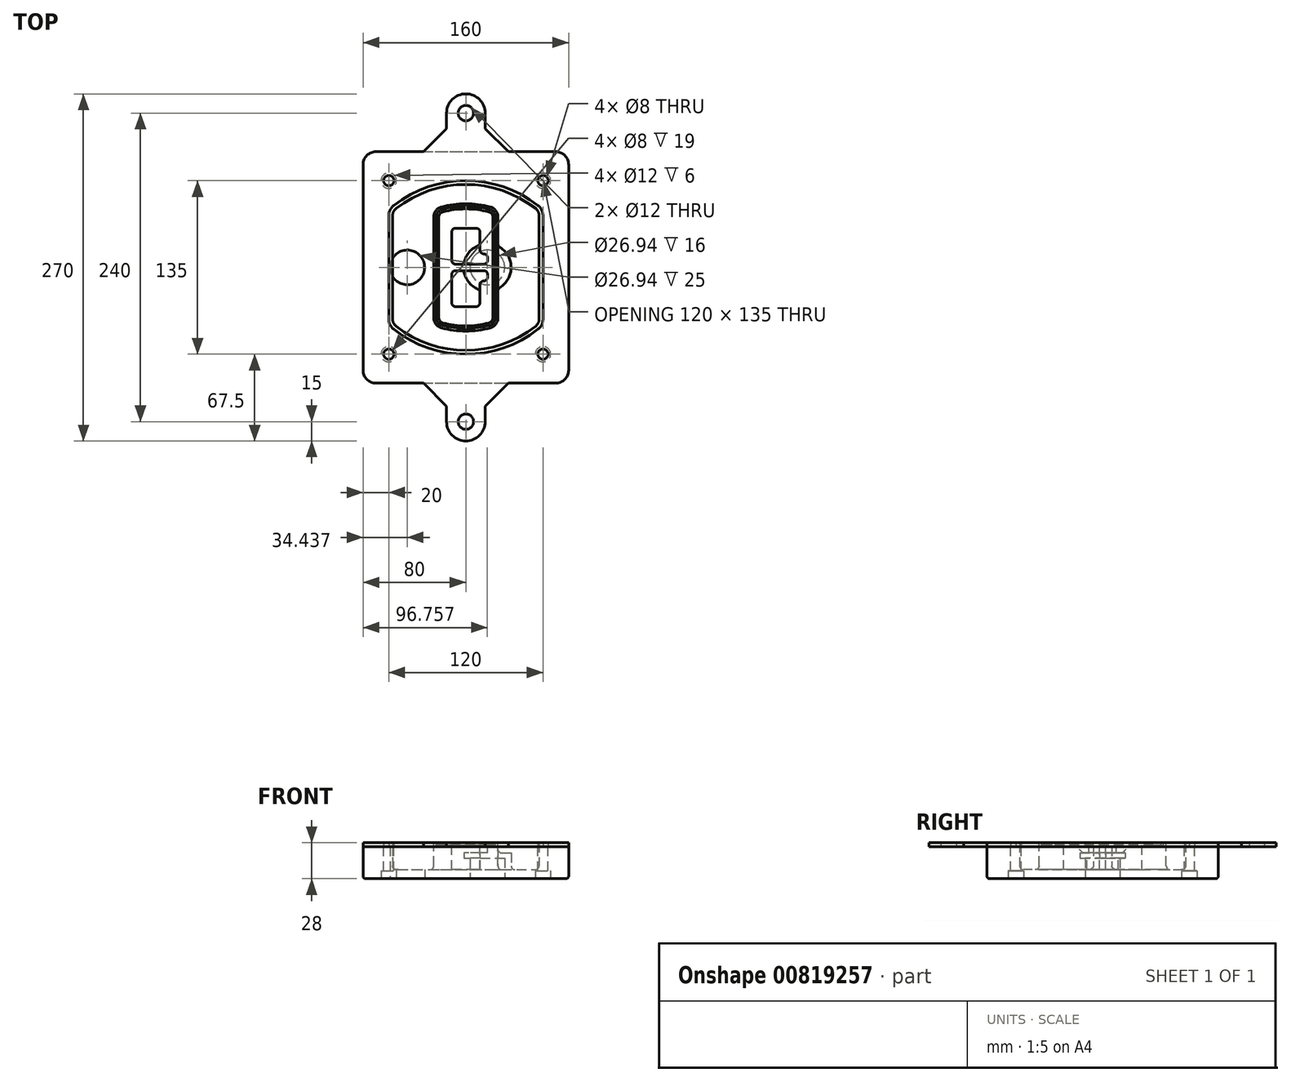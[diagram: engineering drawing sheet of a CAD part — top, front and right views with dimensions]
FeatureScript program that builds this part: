
annotation { "Feature Type Name" : "Feature", "Feature Type Description" : "" }
export const myFeature = defineFeature(function(context is Context, id is Id, definition is map)
    precondition{}
    {
        {
            var Q0;
            Q0=qCreatedBy(makeId("Top.planeOp"),FACE);
            var sketch = newSketch(context, id + "F0", { "sketchPlane" : qUnion([Q0])});
            skPoint(sketch, "E0.rect.middle", {"position": v(0, 0) * mm});
            skLineSegment(sketch, "E1.bottom", {"start": v(-70, -90) * mm, "end": v(70, -90) * mm});
            skLineSegment(sketch, "E1.top", {"start": v(-70, 90) * mm, "end": v(70, 90) * mm});
            skLineSegment(sketch, "E1.left", {"start": v(-80, -80) * mm, "end": v(-80, 80) * mm});
            skLineSegment(sketch, "E1.right", {"start": v(80, -80) * mm, "end": v(80, 80) * mm});
            skLineSegment(sketch, "E2", {"start": v(-80, 90) * mm, "end": v(80, -90) * mm, "construction": true});
            skLineSegment(sketch, "E3", {"start": v(80, 90) * mm, "end": v(-80, -90) * mm, "construction": true});
            skCircle(sketch, "E4", {"center": v(-60, 67.5) * mm, "radius": 4 * mm});
            skCircle(sketch, "E5", {"center": v(60, 67.5) * mm, "radius": 4 * mm});
            skCircle(sketch, "E6", {"center": v(60, -67.5) * mm, "radius": 4 * mm});
            skCircle(sketch, "E7", {"center": v(-60, -67.5) * mm, "radius": 4 * mm});
            skLineSegment(sketch, "E8", {"start": v(-60, 67.5) * mm, "end": v(60, 67.5) * mm, "construction": true});
            skLineSegment(sketch, "E9", {"start": v(60, 67.5) * mm, "end": v(60, -67.5) * mm, "construction": true});
            skLineSegment(sketch, "E10", {"start": v(60, -67.5) * mm, "end": v(-60, -67.5) * mm, "construction": true});
            skLineSegment(sketch, "E11", {"start": v(-60, -67.5) * mm, "end": v(-60, 67.5) * mm, "construction": true});
            skLineSegment(sketch, "E12", {"start": v(-60, 40.3) * mm, "end": v(-60, -40.3) * mm});
            skLineSegment(sketch, "E13", {"start": v(60, 40.3) * mm, "end": v(60, -40.3) * mm});
            skArc(sketch, "E14", {"start": v(56.15, 48.18) * mm, "mid": v(0, 67.5) * mm, "end": v(-56.15, 48.18) * mm});
            skArc(sketch, "E15", {"start": v(-56.15, -48.18) * mm, "mid": v(0, -67.5) * mm, "end": v(56.15, -48.18) * mm});
            skLineSegment(sketch, "E16", {"start": v(-60, 0) * mm, "end": v(60, 0) * mm, "construction": true});
            skPoint(sketch, "E17.visualSharp", {"position": v(-60, -45) * mm});
            skArc(sketch, "E17.filletArc", {"start": v(-60, -40.3) * mm, "mid": v(-58.99, -44.68) * mm, "end": v(-56.15, -48.18) * mm});
            skPoint(sketch, "E18.visualSharp", {"position": v(-60, 45) * mm});
            skArc(sketch, "E18.filletArc", {"start": v(-56.15, 48.18) * mm, "mid": v(-58.99, 44.68) * mm, "end": v(-60, 40.3) * mm});
            skPoint(sketch, "E19.visualSharp", {"position": v(60, 45) * mm});
            skArc(sketch, "E19.filletArc", {"start": v(60, 40.3) * mm, "mid": v(58.99, 44.68) * mm, "end": v(56.15, 48.18) * mm});
            skPoint(sketch, "E20.visualSharp", {"position": v(60, -45) * mm});
            skArc(sketch, "E20.filletArc", {"start": v(56.15, -48.18) * mm, "mid": v(58.99, -44.68) * mm, "end": v(60, -40.3) * mm});
            skPoint(sketch, "E21.visualSharp", {"position": v(-80, 90) * mm});
            skArc(sketch, "E21.filletArc", {"start": v(-70, 90) * mm, "mid": v(-77.07, 87.07) * mm, "end": v(-80, 80) * mm});
            skPoint(sketch, "E22.visualSharp", {"position": v(80, 90) * mm});
            skArc(sketch, "E22.filletArc", {"start": v(80, 80) * mm, "mid": v(77.07, 87.07) * mm, "end": v(70, 90) * mm});
            skPoint(sketch, "E23.visualSharp", {"position": v(80, -90) * mm});
            skArc(sketch, "E23.filletArc", {"start": v(70, -90) * mm, "mid": v(77.07, -87.07) * mm, "end": v(80, -80) * mm});
            skPoint(sketch, "E24.visualSharp", {"position": v(-80, -90) * mm});
            skArc(sketch, "E24.filletArc", {"start": v(-80, -80) * mm, "mid": v(-77.07, -87.07) * mm, "end": v(-70, -90) * mm});
            skArc(sketch, "E25.0", {"start": v(57, 40.3) * mm, "mid": v(56.3, 43.36) * mm, "end": v(54.3, 45.81) * mm});
            skLineSegment(sketch, "E25.1", {"start": v(57, 40.3) * mm, "end": v(57, -40.3) * mm});
            skArc(sketch, "E25.2", {"start": v(54.3, -45.81) * mm, "mid": v(56.3, -43.36) * mm, "end": v(57, -40.3) * mm});
            skArc(sketch, "E25.3", {"start": v(-54.3, -45.81) * mm, "mid": v(0, -64.5) * mm, "end": v(54.3, -45.81) * mm});
            skArc(sketch, "E25.4", {"start": v(-57, -40.3) * mm, "mid": v(-56.3, -43.36) * mm, "end": v(-54.3, -45.81) * mm});
            skArc(sketch, "E25.5", {"start": v(54.3, 45.81) * mm, "mid": v(0, 64.5) * mm, "end": v(-54.3, 45.81) * mm});
            skLineSegment(sketch, "E25.6", {"start": v(-57, 40.3) * mm, "end": v(-57, -40.3) * mm});
            skArc(sketch, "E25.7", {"start": v(-54.3, 45.81) * mm, "mid": v(-56.3, 43.36) * mm, "end": v(-57, 40.3) * mm});
            skArc(sketch, "E26.0", {"start": v(-58.62, 51.33) * mm, "mid": v(-62.58, 46.43) * mm, "end": v(-64, 40.3) * mm});
            skArc(sketch, "E26.1", {"start": v(58.62, 51.33) * mm, "mid": v(0, 71.5) * mm, "end": v(-58.62, 51.33) * mm});
            skArc(sketch, "E26.2", {"start": v(64, 40.3) * mm, "mid": v(62.58, 46.43) * mm, "end": v(58.62, 51.33) * mm});
            skLineSegment(sketch, "E26.3", {"start": v(64, 40.3) * mm, "end": v(64, -40.3) * mm});
            skArc(sketch, "E26.4", {"start": v(58.62, -51.33) * mm, "mid": v(62.58, -46.43) * mm, "end": v(64, -40.3) * mm});
            skLineSegment(sketch, "E26.5", {"start": v(-64, 40.3) * mm, "end": v(-64, -40.3) * mm});
            skArc(sketch, "E26.6", {"start": v(-58.62, -51.33) * mm, "mid": v(0, -71.5) * mm, "end": v(58.62, -51.33) * mm});
            skArc(sketch, "E26.7", {"start": v(-64, -40.3) * mm, "mid": v(-62.58, -46.43) * mm, "end": v(-58.62, -51.33) * mm});
            skSolve(sketch);
        }
        {
            var Q0;
            Q0=makeQuery(id+"F0.imprint","IMPRINT",FACE,{"disambiguationData":[TD([[makeQuery(id+"F0.imprint","IMPRINT",EDGE,{"derivedFrom":sQuery(id+"F0.wireOp",EDGE,"E1.bottom")}),1.0]])]});
            var Q1;
            Q1=makeQuery(id+"F0.imprint","IMPRINT",FACE,{"disambiguationData":[TD([[makeQuery(id+"F0.imprint","IMPRINT",EDGE,{"derivedFrom":sQuery(id+"F0.wireOp",EDGE,"E12")}),1.0]])]});
            var Q2;
            Q2=makeQuery(id+"F0.imprint","IMPRINT",FACE,{"disambiguationData":[TD([[makeQuery(id+"F0.imprint","IMPRINT",EDGE,{"derivedFrom":sQuery(id+"F0.wireOp",EDGE,"E25.0")}),1.0]])]});
            var Q3;
            Q3=makeQuery(id+"F0.imprint","IMPRINT",FACE,{"disambiguationData":[TD([[makeQuery(id+"F0.imprint","IMPRINT",EDGE,{"derivedFrom":sQuery(id+"F0.wireOp",EDGE,"E12")}),-1.0]])]});
            extrude(context, id + "F1", {"entities" : qUnion([Q0, Q1, Q2, Q3]), "oppositeDirection" : true, "depth" : 25 * mm});
        }
        {
            var Q0;
            Q0=makeQuery(id+"F0.imprint","IMPRINT",FACE,{"disambiguationData":[TD([[makeQuery(id+"F0.imprint","IMPRINT",EDGE,{"derivedFrom":sQuery(id+"F0.wireOp",EDGE,"E12")}),1.0]])]});
            extrude(context, id + "F2", {"entities" : qUnion([Q0]), "operationType" : NewBodyOperationType.ADD, "depth" : 3 * mm});
        }
        {
            var Q0;
            Q0=makeQuery(id+"F0.imprint","IMPRINT",FACE,{"disambiguationData":[TD([[makeQuery(id+"F0.imprint","IMPRINT",EDGE,{"derivedFrom":sQuery(id+"F0.wireOp",EDGE,"E25.0")}),1.0]])]});
            extrude(context, id + "F3", {"entities" : qUnion([Q0]), "operationType" : NewBodyOperationType.REMOVE, "oppositeDirection" : true, "depth" : 18 * mm});
        }
        {
            var Q0;
            Q0=makeQuery(id+"F2.opExtrude","CAP_FACE",FACE,{"disambiguationData":[OSD([sQuery(id+"F0.wireOp",EDGE,"E12"),sQuery(id+"F0.wireOp",EDGE,"E13"),sQuery(id+"F0.wireOp",EDGE,"E14"),sQuery(id+"F0.wireOp",EDGE,"E15"),sQuery(id+"F0.wireOp",EDGE,"E17.filletArc"),sQuery(id+"F0.wireOp",EDGE,"E18.filletArc"),sQuery(id+"F0.wireOp",EDGE,"E19.filletArc"),sQuery(id+"F0.wireOp",EDGE,"E20.filletArc"),sQuery(id+"F0.wireOp",EDGE,"E25.0"),sQuery(id+"F0.wireOp",EDGE,"E25.1"),sQuery(id+"F0.wireOp",EDGE,"E25.2"),sQuery(id+"F0.wireOp",EDGE,"E25.3"),sQuery(id+"F0.wireOp",EDGE,"E25.4"),sQuery(id+"F0.wireOp",EDGE,"E25.5"),sQuery(id+"F0.wireOp",EDGE,"E25.6"),sQuery(id+"F0.wireOp",EDGE,"E25.7")])],"isStart":false});
            var sketch = newSketch(context, id + "F4", { "sketchPlane" : qUnion([Q0])});
            skArc(sketch, "E27.0", {"start": v(-19.08, -46.97) * mm, "mid": v(0, -49.5) * mm, "end": v(19.08, -46.97) * mm});
            skArc(sketch, "E28.0", {"start": v(19.08, 46.97) * mm, "mid": v(0, 49.5) * mm, "end": v(-19.08, 46.97) * mm});
            skLineSegment(sketch, "E29", {"start": v(-25, 39.25) * mm, "end": v(-25, -39.25) * mm});
            skLineSegment(sketch, "E30", {"start": v(25, 39.25) * mm, "end": v(25, -39.25) * mm});
            skLineSegment(sketch, "E31", {"start": v(-25, 45.1) * mm, "end": v(25, 45.1) * mm, "construction": true});
            skLineSegment(sketch, "E32", {"start": v(-25, -45.1) * mm, "end": v(25, -45.1) * mm, "construction": true});
            skPoint(sketch, "E33.visualSharp", {"position": v(-25, 45.1) * mm});
            skArc(sketch, "E33.filletArc", {"start": v(-19.08, 46.97) * mm, "mid": v(-23.35, 44.11) * mm, "end": v(-25, 39.25) * mm});
            skPoint(sketch, "E34.visualSharp", {"position": v(25, 45.1) * mm});
            skArc(sketch, "E34.filletArc", {"start": v(25, 39.25) * mm, "mid": v(23.35, 44.11) * mm, "end": v(19.08, 46.97) * mm});
            skPoint(sketch, "E35.visualSharp", {"position": v(25, -45.1) * mm});
            skArc(sketch, "E35.filletArc", {"start": v(19.08, -46.97) * mm, "mid": v(23.35, -44.11) * mm, "end": v(25, -39.25) * mm});
            skPoint(sketch, "E36.visualSharp", {"position": v(-25, -45.1) * mm});
            skArc(sketch, "E36.filletArc", {"start": v(-25, -39.25) * mm, "mid": v(-23.35, -44.11) * mm, "end": v(-19.08, -46.97) * mm});
            skArc(sketch, "E37.0", {"start": v(54.3, 45.81) * mm, "mid": v(0, 64.5) * mm, "end": v(-54.3, 45.81) * mm});
            skArc(sketch, "E37.1", {"start": v(-54.3, 45.81) * mm, "mid": v(-56.3, 43.36) * mm, "end": v(-57, 40.3) * mm});
            skLineSegment(sketch, "E37.2", {"start": v(-57, 40.3) * mm, "end": v(-57, -40.3) * mm});
            skArc(sketch, "E37.3", {"start": v(-57, -40.3) * mm, "mid": v(-56.3, -43.36) * mm, "end": v(-54.3, -45.81) * mm});
            skArc(sketch, "E37.4", {"start": v(-54.3, -45.81) * mm, "mid": v(0, -64.5) * mm, "end": v(54.3, -45.81) * mm});
            skArc(sketch, "E37.5", {"start": v(54.3, -45.81) * mm, "mid": v(56.3, -43.36) * mm, "end": v(57, -40.3) * mm});
            skLineSegment(sketch, "E37.6", {"start": v(57, 40.3) * mm, "end": v(57, -40.3) * mm});
            skArc(sketch, "E37.7", {"start": v(57, 40.3) * mm, "mid": v(56.3, 43.36) * mm, "end": v(54.3, 45.81) * mm});
            skLineSegment(sketch, "E38.0", {"start": v(23, 39.25) * mm, "end": v(23, -39.25) * mm});
            skArc(sketch, "E38.1", {"start": v(18.56, -45.04) * mm, "mid": v(21.76, -42.9) * mm, "end": v(23, -39.25) * mm});
            skArc(sketch, "E38.2", {"start": v(-18.56, -45.04) * mm, "mid": v(0, -47.5) * mm, "end": v(18.56, -45.04) * mm});
            skArc(sketch, "E38.3", {"start": v(-23, -39.25) * mm, "mid": v(-21.76, -42.9) * mm, "end": v(-18.56, -45.04) * mm});
            skLineSegment(sketch, "E38.4", {"start": v(-23, 39.25) * mm, "end": v(-23, -39.25) * mm});
            skArc(sketch, "E38.5", {"start": v(23, 39.25) * mm, "mid": v(21.76, 42.9) * mm, "end": v(18.56, 45.04) * mm});
            skArc(sketch, "E38.6", {"start": v(-18.56, 45.04) * mm, "mid": v(-21.76, 42.9) * mm, "end": v(-23, 39.25) * mm});
            skArc(sketch, "E38.7", {"start": v(18.56, 45.04) * mm, "mid": v(0, 47.5) * mm, "end": v(-18.56, 45.04) * mm});
            skArc(sketch, "E39.0", {"start": v(21, 39.25) * mm, "mid": v(20.18, 41.68) * mm, "end": v(18.04, 43.1) * mm});
            skLineSegment(sketch, "E39.1", {"start": v(21, 39.25) * mm, "end": v(21, -39.25) * mm});
            skArc(sketch, "E39.2", {"start": v(18.04, -43.1) * mm, "mid": v(20.18, -41.68) * mm, "end": v(21, -39.25) * mm});
            skArc(sketch, "E39.3", {"start": v(-18.04, -43.1) * mm, "mid": v(0, -45.5) * mm, "end": v(18.04, -43.1) * mm});
            skArc(sketch, "E39.4", {"start": v(-21, -39.25) * mm, "mid": v(-20.18, -41.68) * mm, "end": v(-18.04, -43.1) * mm});
            skArc(sketch, "E39.5", {"start": v(18.04, 43.1) * mm, "mid": v(0, 45.5) * mm, "end": v(-18.04, 43.1) * mm});
            skLineSegment(sketch, "E39.6", {"start": v(-21, 39.25) * mm, "end": v(-21, -39.25) * mm});
            skArc(sketch, "E39.7", {"start": v(-18.04, 43.1) * mm, "mid": v(-20.18, 41.68) * mm, "end": v(-21, 39.25) * mm});
            skLineSegment(sketch, "E40", {"start": v(-25, 0) * mm, "end": v(25, 0) * mm, "construction": true});
            skLineSegment(sketch, "E41", {"start": v(-11, 5.5) * mm, "end": v(-11, 27.5) * mm});
            skLineSegment(sketch, "E42", {"start": v(-8, 30.5) * mm, "end": v(8, 30.5) * mm});
            skLineSegment(sketch, "E43", {"start": v(11, 27.5) * mm, "end": v(11, 13.5) * mm});
            skLineSegment(sketch, "E44", {"start": v(14, 10.5) * mm, "end": v(14, 10.5) * mm});
            skLineSegment(sketch, "E45", {"start": v(17, 7.5) * mm, "end": v(17, 5.5) * mm});
            skLineSegment(sketch, "E46", {"start": v(14, 2.5) * mm, "end": v(-8, 2.5) * mm});
            skPoint(sketch, "E47.visualSharp", {"position": v(-11, 30.5) * mm});
            skArc(sketch, "E47.filletArc", {"start": v(-8, 30.5) * mm, "mid": v(-10.12, 29.62) * mm, "end": v(-11, 27.5) * mm});
            skPoint(sketch, "E48.visualSharp", {"position": v(11, 30.5) * mm});
            skArc(sketch, "E48.filletArc", {"start": v(11, 27.5) * mm, "mid": v(10.12, 29.62) * mm, "end": v(8, 30.5) * mm});
            skPoint(sketch, "E49.visualSharp", {"position": v(11, 10.5) * mm});
            skArc(sketch, "E49.filletArc", {"start": v(11, 13.5) * mm, "mid": v(11.88, 11.38) * mm, "end": v(14, 10.5) * mm});
            skPoint(sketch, "E50.visualSharp", {"position": v(17, 10.5) * mm});
            skArc(sketch, "E50.filletArc", {"start": v(17, 7.5) * mm, "mid": v(16.12, 9.62) * mm, "end": v(14, 10.5) * mm});
            skPoint(sketch, "E51.visualSharp", {"position": v(17, 2.5) * mm});
            skArc(sketch, "E51.filletArc", {"start": v(14, 2.5) * mm, "mid": v(16.12, 3.38) * mm, "end": v(17, 5.5) * mm});
            skPoint(sketch, "E52.visualSharp", {"position": v(-11, 2.5) * mm});
            skArc(sketch, "E52.filletArc", {"start": v(-11, 5.5) * mm, "mid": v(-10.12, 3.38) * mm, "end": v(-8, 2.5) * mm});
            skLineSegment(sketch, "E53.0.MirrorCS", {"start": v(14, -2.5) * mm, "end": v(-8, -2.5) * mm});
            skArc(sketch, "E54.0.MirrorCS", {"start": v(-11, -5.5) * mm, "mid": v(-10.12, -3.38) * mm, "end": v(-8, -2.5) * mm});
            skLineSegment(sketch, "E55.0.MirrorCS", {"start": v(-11, -5.5) * mm, "end": v(-11, -27.5) * mm});
            skArc(sketch, "E56.0.MirrorCS", {"start": v(-8, -30.5) * mm, "mid": v(-10.12, -29.62) * mm, "end": v(-11, -27.5) * mm});
            skLineSegment(sketch, "E57.0.MirrorCS", {"start": v(-8, -30.5) * mm, "end": v(8, -30.5) * mm});
            skArc(sketch, "E58.0.MirrorCS", {"start": v(11, -27.5) * mm, "mid": v(10.12, -29.62) * mm, "end": v(8, -30.5) * mm});
            skLineSegment(sketch, "E59.0.MirrorCS", {"start": v(11, -27.5) * mm, "end": v(11, -13.5) * mm});
            skArc(sketch, "E60.0.MirrorCS", {"start": v(11, -13.5) * mm, "mid": v(11.88, -11.38) * mm, "end": v(14, -10.5) * mm});
            skArc(sketch, "E61.0.MirrorCS", {"start": v(17, -7.5) * mm, "mid": v(16.12, -9.62) * mm, "end": v(14, -10.5) * mm});
            skLineSegment(sketch, "E62.0.MirrorCS", {"start": v(17, -7.5) * mm, "end": v(17, -5.5) * mm});
            skArc(sketch, "E63.0.MirrorCS", {"start": v(14, -2.5) * mm, "mid": v(16.12, -3.38) * mm, "end": v(17, -5.5) * mm});
            skSolve(sketch);
        }
        {
            var Q0;
            Q0=makeQuery(id+"F4.imprint","IMPRINT",FACE,{"disambiguationData":[TD([[makeQuery(id+"F4.imprint","IMPRINT",EDGE,{"derivedFrom":sQuery(id+"F4.wireOp",EDGE,"E27.0")}),1.0]])]});
            var Q1;
            Q1=makeQuery(id+"F4.imprint","IMPRINT",FACE,{"disambiguationData":[TD([[makeQuery(id+"F4.imprint","IMPRINT",EDGE,{"derivedFrom":sQuery(id+"F4.wireOp",EDGE,"E38.0")}),-1.0]])]});
            var Q2;
            Q2=makeQuery(id+"F4.imprint","IMPRINT",FACE,{"disambiguationData":[TD([[makeQuery(id+"F4.imprint","IMPRINT",EDGE,{"derivedFrom":sQuery(id+"F4.wireOp",EDGE,"E39.0")}),1.0]])]});
            extrude(context, id + "F5", {"entities" : qUnion([Q0, Q1, Q2]), "operationType" : NewBodyOperationType.ADD, "endBound" : BoundingType.UP_TO_NEXT, "oppositeDirection" : true, "depth" : 25 * mm});
        }
        {
            var Q0;
            Q0=makeQuery(id+"F4.imprint","IMPRINT",FACE,{"disambiguationData":[TD([[makeQuery(id+"F4.imprint","IMPRINT",EDGE,{"derivedFrom":sQuery(id+"F4.wireOp",EDGE,"E38.0")}),-1.0]])]});
            extrude(context, id + "F6", {"entities" : qUnion([Q0]), "operationType" : NewBodyOperationType.REMOVE, "oppositeDirection" : true, "depth" : 2 * mm});
        }
        {
            var Q0;
            Q0=makeQuery(id+"F1.opExtrude","CAP_FACE",FACE,{"disambiguationData":[OSD([sQuery(id+"F0.wireOp",EDGE,"E1.bottom"),sQuery(id+"F0.wireOp",EDGE,"E1.top"),sQuery(id+"F0.wireOp",EDGE,"E1.left"),sQuery(id+"F0.wireOp",EDGE,"E1.right"),sQuery(id+"F0.wireOp",EDGE,"E4"),sQuery(id+"F0.wireOp",EDGE,"E5"),sQuery(id+"F0.wireOp",EDGE,"E6"),sQuery(id+"F0.wireOp",EDGE,"E7"),sQuery(id+"F0.wireOp",EDGE,"E21.filletArc"),sQuery(id+"F0.wireOp",EDGE,"E22.filletArc"),sQuery(id+"F0.wireOp",EDGE,"E23.filletArc"),sQuery(id+"F0.wireOp",EDGE,"E24.filletArc")])],"isStart":false});
            var sketch = newSketch(context, id + "F7", { "sketchPlane" : qUnion([Q0])});
            skCircle(sketch, "E64", {"center": v(16.76, 0) * mm, "radius": 13.47 * mm});
            skCircle(sketch, "E65", {"center": v(-45.56, 0) * mm, "radius": 13.47 * mm});
            skLineSegment(sketch, "E66", {"start": v(80, 0) * mm, "end": v(-80, 0) * mm});
            skCircle(sketch, "E67", {"center": v(16.76, 0) * mm, "radius": 18.47 * mm});
            skCircle(sketch, "E68", {"center": v(60, -67.5) * mm, "radius": 6 * mm});
            skCircle(sketch, "E69", {"center": v(-60, -67.5) * mm, "radius": 6 * mm});
            skCircle(sketch, "E70", {"center": v(-60, 67.5) * mm, "radius": 6 * mm});
            skCircle(sketch, "E71", {"center": v(60, 67.5) * mm, "radius": 6 * mm});
            skSolve(sketch);
        }
        {
            var Q0;
            {var subQ1=sQuery(id+"F7.wireOp",EDGE,"E66");var subQ4=sQuery(id+"F7.wireOp",EDGE,"E64");var subQ6=makeQuery(id+"F7.imprint","INTERSECT",VERTEX,{"disambiguationData":[OD(0.0)],"derivedFrom":[subQ4,subQ1]});Q0=makeQuery(id+"F7.imprint","IMPRINT",FACE,{"disambiguationData":[TD([[makeQuery(id+"F7.imprint","IMPRINT",EDGE,{"disambiguationData":[TD([[subQ6,-1.0]])],"derivedFrom":subQ4}),-1.0]])]});}
            var Q1;
            {var subQ0=sQuery(id+"F7.wireOp",EDGE,"E66");var subQ1=sQuery(id+"F7.wireOp",EDGE,"E64");var subQ3=makeQuery(id+"F7.imprint","INTERSECT",VERTEX,{"disambiguationData":[OD(0.0)],"derivedFrom":[subQ1,subQ0]});Q1=makeQuery(id+"F7.imprint","IMPRINT",FACE,{"disambiguationData":[TD([[makeQuery(id+"F7.imprint","IMPRINT",EDGE,{"disambiguationData":[TD([[subQ3,-1.0]])],"derivedFrom":subQ1}),1.0]])]});}
            var Q2;
            {var subQ0=sQuery(id+"F7.wireOp",EDGE,"E66");var subQ1=sQuery(id+"F7.wireOp",EDGE,"E64");var subQ3=makeQuery(id+"F7.imprint","INTERSECT",VERTEX,{"disambiguationData":[OD(0.0)],"derivedFrom":[subQ1,subQ0]});Q2=makeQuery(id+"F7.imprint","IMPRINT",FACE,{"disambiguationData":[TD([[makeQuery(id+"F7.imprint","IMPRINT",EDGE,{"disambiguationData":[TD([[subQ3,1.0]])],"derivedFrom":subQ1}),1.0]])]});}
            var Q3;
            {var subQ1=sQuery(id+"F7.wireOp",EDGE,"E66");var subQ4=sQuery(id+"F7.wireOp",EDGE,"E64");var subQ6=makeQuery(id+"F7.imprint","INTERSECT",VERTEX,{"disambiguationData":[OD(0.0)],"derivedFrom":[subQ4,subQ1]});Q3=makeQuery(id+"F7.imprint","IMPRINT",FACE,{"disambiguationData":[TD([[makeQuery(id+"F7.imprint","IMPRINT",EDGE,{"disambiguationData":[TD([[subQ6,1.0]])],"derivedFrom":subQ4}),-1.0]])]});}
            extrude(context, id + "F8", {"entities" : qUnion([Q0, Q1, Q2, Q3]), "operationType" : NewBodyOperationType.ADD, "oppositeDirection" : true, "depth" : 20 * mm});
        }
        {
            var Q0;
            {var subQ0=sQuery(id+"F7.wireOp",EDGE,"E66");var subQ1=sQuery(id+"F7.wireOp",EDGE,"E64");var subQ3=makeQuery(id+"F7.imprint","INTERSECT",VERTEX,{"disambiguationData":[OD(0.0)],"derivedFrom":[subQ1,subQ0]});Q0=makeQuery(id+"F7.imprint","IMPRINT",FACE,{"disambiguationData":[TD([[makeQuery(id+"F7.imprint","IMPRINT",EDGE,{"disambiguationData":[TD([[subQ3,-1.0]])],"derivedFrom":subQ1}),1.0]])]});}
            var Q1;
            {var subQ0=sQuery(id+"F7.wireOp",EDGE,"E66");var subQ1=sQuery(id+"F7.wireOp",EDGE,"E64");var subQ3=makeQuery(id+"F7.imprint","INTERSECT",VERTEX,{"disambiguationData":[OD(0.0)],"derivedFrom":[subQ1,subQ0]});Q1=makeQuery(id+"F7.imprint","IMPRINT",FACE,{"disambiguationData":[TD([[makeQuery(id+"F7.imprint","IMPRINT",EDGE,{"disambiguationData":[TD([[subQ3,1.0]])],"derivedFrom":subQ1}),1.0]])]});}
            extrude(context, id + "F9", {"entities" : qUnion([Q0, Q1]), "operationType" : NewBodyOperationType.REMOVE, "oppositeDirection" : true, "depth" : 16 * mm});
        }
        {
            var Q0;
            {var subQ0=sQuery(id+"F7.wireOp",EDGE,"E66");var subQ1=sQuery(id+"F7.wireOp",EDGE,"E65");var subQ3=makeQuery(id+"F7.imprint","INTERSECT",VERTEX,{"disambiguationData":[OD(0.0)],"derivedFrom":[subQ1,subQ0]});Q0=makeQuery(id+"F7.imprint","IMPRINT",FACE,{"disambiguationData":[TD([[makeQuery(id+"F7.imprint","IMPRINT",EDGE,{"disambiguationData":[TD([[subQ3,-1.0]])],"derivedFrom":subQ1}),1.0]])]});}
            var Q1;
            {var subQ0=sQuery(id+"F7.wireOp",EDGE,"E66");var subQ1=sQuery(id+"F7.wireOp",EDGE,"E65");var subQ3=makeQuery(id+"F7.imprint","INTERSECT",VERTEX,{"disambiguationData":[OD(0.0)],"derivedFrom":[subQ1,subQ0]});Q1=makeQuery(id+"F7.imprint","IMPRINT",FACE,{"disambiguationData":[TD([[makeQuery(id+"F7.imprint","IMPRINT",EDGE,{"disambiguationData":[TD([[subQ3,1.0]])],"derivedFrom":subQ1}),1.0]])]});}
            extrude(context, id + "F10", {"entities" : qUnion([Q0, Q1]), "operationType" : NewBodyOperationType.REMOVE, "oppositeDirection" : true, "depth" : 25 * mm});
        }
        {
            var Q0;
            Q0=makeQuery(id+"F7.imprint","IMPRINT",FACE,{"disambiguationData":[TD([[makeQuery(id+"F7.imprint","IMPRINT",EDGE,{"derivedFrom":sQuery(id+"F7.wireOp",EDGE,"E68")}),1.0]])]});
            var Q1;
            Q1=makeQuery(id+"F7.imprint","IMPRINT",FACE,{"disambiguationData":[TD([[makeQuery(id+"F7.imprint","IMPRINT",EDGE,{"derivedFrom":makeQuery(id+"F1.opExtrude","CAP_EDGE",EDGE,{"disambiguationData":[OSD([sQuery(id+"F0.wireOp",EDGE,"E5")])],"isStart":false})}),-1.0]])]});
            var Q2;
            Q2=makeQuery(id+"F7.imprint","IMPRINT",FACE,{"disambiguationData":[TD([[makeQuery(id+"F7.imprint","IMPRINT",EDGE,{"derivedFrom":sQuery(id+"F7.wireOp",EDGE,"E69")}),1.0]])]});
            var Q3;
            Q3=makeQuery(id+"F7.imprint","IMPRINT",FACE,{"disambiguationData":[TD([[makeQuery(id+"F7.imprint","IMPRINT",EDGE,{"derivedFrom":makeQuery(id+"F1.opExtrude","CAP_EDGE",EDGE,{"disambiguationData":[OSD([sQuery(id+"F0.wireOp",EDGE,"E4")])],"isStart":false})}),-1.0]])]});
            var Q4;
            Q4=makeQuery(id+"F7.imprint","IMPRINT",FACE,{"disambiguationData":[TD([[makeQuery(id+"F7.imprint","IMPRINT",EDGE,{"derivedFrom":sQuery(id+"F7.wireOp",EDGE,"E70")}),1.0]])]});
            var Q5;
            Q5=makeQuery(id+"F7.imprint","IMPRINT",FACE,{"disambiguationData":[TD([[makeQuery(id+"F7.imprint","IMPRINT",EDGE,{"derivedFrom":makeQuery(id+"F1.opExtrude","CAP_EDGE",EDGE,{"disambiguationData":[OSD([sQuery(id+"F0.wireOp",EDGE,"E7")])],"isStart":false})}),-1.0]])]});
            var Q6;
            Q6=makeQuery(id+"F7.imprint","IMPRINT",FACE,{"disambiguationData":[TD([[makeQuery(id+"F7.imprint","IMPRINT",EDGE,{"derivedFrom":sQuery(id+"F7.wireOp",EDGE,"E71")}),1.0]])]});
            var Q7;
            Q7=makeQuery(id+"F7.imprint","IMPRINT",FACE,{"disambiguationData":[TD([[makeQuery(id+"F7.imprint","IMPRINT",EDGE,{"derivedFrom":makeQuery(id+"F1.opExtrude","CAP_EDGE",EDGE,{"disambiguationData":[OSD([sQuery(id+"F0.wireOp",EDGE,"E6")])],"isStart":false})}),-1.0]])]});
            extrude(context, id + "F11", {"entities" : qUnion([Q0, Q1, Q2, Q3, Q4, Q5, Q6, Q7]), "operationType" : NewBodyOperationType.REMOVE, "oppositeDirection" : true, "depth" : 6 * mm});
        }
        {
            var Q0;
            Q0=makeQuery(id+"F9.boolean.opBoolean","COPY",FACE,{"derivedFrom":makeQuery(id+"F9.opExtrude","CAP_FACE",FACE,{"disambiguationData":[OSD([sQuery(id+"F7.wireOp",EDGE,"E64")])],"isStart":false})});
            var sketch = newSketch(context, id + "F12", { "sketchPlane" : qUnion([Q0])});
            skArc(sketch, "E72.0", {"start": v(11, 17.55) * mm, "mid": v(2.57, 11.82) * mm, "end": v(-1.54, 2.5) * mm});
            skArc(sketch, "E72.1", {"start": v(-1.54, -2.5) * mm, "mid": v(2.57, -11.82) * mm, "end": v(11, -17.55) * mm});
            skLineSegment(sketch, "E73", {"start": v(-1.54, -2.5) * mm, "end": v(14, -2.5) * mm});
            skLineSegment(sketch, "E74.0", {"start": v(14, 2.5) * mm, "end": v(-1.54, 2.5) * mm});
            skArc(sketch, "E74.1", {"start": v(14, 2.5) * mm, "mid": v(16.12, 3.38) * mm, "end": v(17, 5.5) * mm});
            skLineSegment(sketch, "E74.2", {"start": v(17, 7.5) * mm, "end": v(17, 5.5) * mm});
            skArc(sketch, "E74.3", {"start": v(17, 7.5) * mm, "mid": v(16.12, 9.62) * mm, "end": v(14, 10.5) * mm});
            skArc(sketch, "E74.4", {"start": v(11, 13.5) * mm, "mid": v(11.88, 11.38) * mm, "end": v(14, 10.5) * mm});
            skLineSegment(sketch, "E74.5", {"start": v(11, 17.55) * mm, "end": v(11, 13.5) * mm});
            skLineSegment(sketch, "E74.7", {"start": v(14, -2.5) * mm, "end": v(-1.54, -2.5) * mm});
            skArc(sketch, "E74.8", {"start": v(14, -2.5) * mm, "mid": v(16.12, -3.38) * mm, "end": v(17, -5.5) * mm});
            skLineSegment(sketch, "E74.9", {"start": v(17, -7.5) * mm, "end": v(17, -5.5) * mm});
            skArc(sketch, "E74.10", {"start": v(17, -7.5) * mm, "mid": v(16.12, -9.62) * mm, "end": v(14, -10.5) * mm});
            skArc(sketch, "E74.11", {"start": v(11, -13.5) * mm, "mid": v(11.88, -11.38) * mm, "end": v(14, -10.5) * mm});
            skLineSegment(sketch, "E74.12", {"start": v(11, -17.55) * mm, "end": v(11, -13.5) * mm});
            skPoint(sketch, "E75.orphan", {"position": v(11, -27.5) * mm});
            skPoint(sketch, "E76.orphan", {"position": v(-8, -2.5) * mm});
            skPoint(sketch, "E77.orphan", {"position": v(-8, 2.5) * mm});
            skPoint(sketch, "E78.orphan", {"position": v(11, 27.5) * mm});
            skSolve(sketch);
        }
        {
            var Q0;
            {var subQ7=sQuery(id+"F12.wireOp",EDGE,"E72.0");var subQ14=sQuery(id+"F12.wireOp",EDGE,"E72.1");var subQ16=sQuery(id+"F12.wireOp",EDGE,"E74.1");var subQ18=sQuery(id+"F12.wireOp",EDGE,"E74.8");Q0=qUnion([makeQuery(id+"F12.imprint","IMPRINT",FACE,{"disambiguationData":[TD([[makeQuery(id+"F12.imprint","IMPRINT",EDGE,{"derivedFrom":subQ7}),1.0]])]}),makeQuery(id+"F12.imprint","IMPRINT",FACE,{"disambiguationData":[TD([[makeQuery(id+"F12.imprint","IMPRINT",EDGE,{"derivedFrom":subQ14}),1.0]])]}),makeQuery(id+"F12.imprint","IMPRINT",FACE,{"disambiguationData":[TD([[makeQuery(id+"F12.imprint","IMPRINT",EDGE,{"derivedFrom":subQ16}),1.0]])]}),makeQuery(id+"F12.imprint","IMPRINT",FACE,{"disambiguationData":[TD([[makeQuery(id+"F12.imprint","IMPRINT",EDGE,{"derivedFrom":subQ18}),-1.0]])]})]);}
            var Q1;
            Q1=makeQuery(id+"F5.boolean.opBoolean","SPLIT",FACE,{"disambiguationData":[TD([makeQuery(id+"F5.opExtrude","SWEPT_FACE",FACE,{"disambiguationData":[OSD([sQuery(id+"F4.wireOp",EDGE,"E41")])]})])],"derivedFrom":makeQuery(id+"F3.boolean.opBoolean","COPY",FACE,{"derivedFrom":makeQuery(id+"F3.opExtrude","CAP_FACE",FACE,{"disambiguationData":[OSD([sQuery(id+"F0.wireOp",EDGE,"E25.0"),sQuery(id+"F0.wireOp",EDGE,"E25.1"),sQuery(id+"F0.wireOp",EDGE,"E25.2"),sQuery(id+"F0.wireOp",EDGE,"E25.3"),sQuery(id+"F0.wireOp",EDGE,"E25.4"),sQuery(id+"F0.wireOp",EDGE,"E25.5"),sQuery(id+"F0.wireOp",EDGE,"E25.6"),sQuery(id+"F0.wireOp",EDGE,"E25.7")])],"isStart":false})})});
            extrude(context, id + "F13", {"entities" : qUnion([Q0]), "operationType" : NewBodyOperationType.REMOVE, "endBound" : BoundingType.UP_TO_SURFACE, "endBoundEntityFace" : qUnion([Q1]), "depth" : 25 * mm});
        }
        {
            var Q0;
            Q0=makeQuery(id+"F3.boolean.opBoolean","COPY",EDGE,{"derivedFrom":makeQuery(id+"F3.opExtrude","CAP_EDGE",EDGE,{"disambiguationData":[OSD([sQuery(id+"F0.wireOp",EDGE,"E25.6")])],"isStart":false})});
            var Q1;
            Q1=makeQuery(id+"F8.boolean.opBoolean","INTERSECT",EDGE,{"derivedFrom":[makeQuery(id+"F5.opExtrude","SWEPT_FACE",FACE,{"disambiguationData":[OSD([sQuery(id+"F4.wireOp",EDGE,"E30")])]}),makeQuery(id+"F8.opExtrude","CAP_FACE",FACE,{"disambiguationData":[OSD([sQuery(id+"F7.wireOp",EDGE,"E67")])],"isStart":false})]});
            var Q2;
            Q2=makeQuery(id+"F8.boolean.opBoolean","INTERSECT",EDGE,{"disambiguationData":[OD(1.0)],"derivedFrom":[makeQuery(id+"F5.opExtrude","SWEPT_FACE",FACE,{"disambiguationData":[OSD([sQuery(id+"F4.wireOp",EDGE,"E30")])]}),makeQuery(id+"F8.opExtrude","SWEPT_FACE",FACE,{"disambiguationData":[OSD([sQuery(id+"F7.wireOp",EDGE,"E67")])]})]});
            var Q3;
            {var subQ0=sQuery(id+"F4.wireOp",EDGE,"E30");Q3=makeQuery(id+"F8.boolean.opBoolean","SPLIT",EDGE,{"disambiguationData":[TD([makeQuery(id+"F5.opExtrude","SWEPT_FACE",FACE,{"disambiguationData":[OSD([sQuery(id+"F4.wireOp",EDGE,"E35.filletArc")])]})])],"derivedFrom":makeQuery(id+"F5.opExtrude","CAP_EDGE",EDGE,{"disambiguationData":[OSD([subQ0])],"isStart":false})});}
            var Q4;
            {var subQ0=sQuery(id+"F0.wireOp",EDGE,"E25.7");var subQ1=sQuery(id+"F0.wireOp",EDGE,"E25.1");var subQ2=sQuery(id+"F0.wireOp",EDGE,"E25.6");var subQ3=sQuery(id+"F0.wireOp",EDGE,"E25.5");var subQ4=sQuery(id+"F0.wireOp",EDGE,"E25.4");var subQ5=sQuery(id+"F0.wireOp",EDGE,"E25.0");var subQ6=sQuery(id+"F0.wireOp",EDGE,"E25.2");var subQ7=sQuery(id+"F0.wireOp",EDGE,"E25.3");Q4=makeQuery(id+"F8.boolean.opBoolean","INTERSECT",EDGE,{"derivedFrom":[makeQuery(id+"F5.boolean.opBoolean","SPLIT",FACE,{"disambiguationData":[TD([makeQuery(id+"F2.opExtrude","SWEPT_FACE",FACE,{"disambiguationData":[OSD([subQ5])]})])],"derivedFrom":makeQuery(id+"F3.boolean.opBoolean","COPY",FACE,{"derivedFrom":makeQuery(id+"F3.opExtrude","CAP_FACE",FACE,{"disambiguationData":[OSD([subQ5,subQ1,subQ6,subQ7,subQ4,subQ3,subQ2,subQ0])],"isStart":false})})}),makeQuery(id+"F8.opExtrude","SWEPT_FACE",FACE,{"disambiguationData":[OSD([sQuery(id+"F7.wireOp",EDGE,"E67")])]})]});}
            var Q5;
            Q5=makeQuery(id+"F8.boolean.opBoolean","INTERSECT",EDGE,{"disambiguationData":[OD(0.0)],"derivedFrom":[makeQuery(id+"F5.opExtrude","SWEPT_FACE",FACE,{"disambiguationData":[OSD([sQuery(id+"F4.wireOp",EDGE,"E30")])]}),makeQuery(id+"F8.opExtrude","SWEPT_FACE",FACE,{"disambiguationData":[OSD([sQuery(id+"F7.wireOp",EDGE,"E67")])]})]});
            fillet(context, id + "F14", {"entities" : qUnion([Q0, Q1, Q2, Q3, Q4, Q5]), "radius" : 3 * mm, "tangentPropagation" : true, "allowEdgeOverflow" : false});
        }
        {
            var Q0;
            Q0=makeQuery(id+"F1.opExtrude","CAP_EDGE",EDGE,{"disambiguationData":[OSD([sQuery(id+"F0.wireOp",EDGE,"E1.bottom")])],"isStart":false});
            fillet(context, id + "F15", {"entities" : qUnion([Q0]), "radius" : 2 * mm, "tangentPropagation" : true, "allowEdgeOverflow" : false});
        }
        {
            var Q0;
            {var subQ0=sQuery(id+"F0.wireOp",EDGE,"E21.filletArc");var subQ1=sQuery(id+"F0.wireOp",EDGE,"E7");var subQ2=sQuery(id+"F0.wireOp",EDGE,"E6");var subQ3=sQuery(id+"F0.wireOp",EDGE,"E5");var subQ4=sQuery(id+"F0.wireOp",EDGE,"E4");var subQ5=sQuery(id+"F0.wireOp",EDGE,"E22.filletArc");var subQ6=sQuery(id+"F0.wireOp",EDGE,"E1.bottom");var subQ7=sQuery(id+"F0.wireOp",EDGE,"E1.right");var subQ8=sQuery(id+"F0.wireOp",EDGE,"E1.top");var subQ9=sQuery(id+"F0.wireOp",EDGE,"E1.left");var subQ10=sQuery(id+"F0.wireOp",EDGE,"E23.filletArc");var subQ11=sQuery(id+"F0.wireOp",EDGE,"E24.filletArc");Q0=makeQuery(id+"F2.boolean.opBoolean","SPLIT",FACE,{"disambiguationData":[TD([makeQuery(id+"F1.opExtrude","SWEPT_FACE",FACE,{"disambiguationData":[OSD([subQ6])]})])],"derivedFrom":makeQuery(id+"F1.opExtrude","CAP_FACE",FACE,{"disambiguationData":[OSD([subQ6,subQ8,subQ9,subQ7,subQ4,subQ3,subQ2,subQ1,subQ0,subQ5,subQ10,subQ11])],"isStart":true})});}
            var sketch = newSketch(context, id + "F16", { "sketchPlane" : qUnion([Q0])});
            skLineSegment(sketch, "E79", {"start": v(0, 90) * mm, "end": v(0, 120) * mm, "construction": true});
            skCircle(sketch, "E80", {"center": v(0, 120) * mm, "radius": 6 * mm});
            skArc(sketch, "E81", {"start": v(15, 120) * mm, "mid": v(0, 135) * mm, "end": v(-15, 120) * mm});
            skLineSegment(sketch, "E82", {"start": v(-15, 120) * mm, "end": v(-15, 108) * mm});
            skLineSegment(sketch, "E83", {"start": v(-15, 108) * mm, "end": v(-33, 90) * mm});
            skLineSegment(sketch, "E84", {"start": v(15, 120) * mm, "end": v(15, 108) * mm});
            skLineSegment(sketch, "E85", {"start": v(15, 108) * mm, "end": v(33, 90) * mm});
            skLineSegment(sketch, "E86", {"start": v(80, 0) * mm, "end": v(-80, 0) * mm, "construction": true});
            skLineSegment(sketch, "E87.MirrorCS", {"start": v(-15, -120) * mm, "end": v(-15, -108) * mm});
            skLineSegment(sketch, "E88.MirrorCS", {"start": v(15, -108) * mm, "end": v(33, -90) * mm});
            skArc(sketch, "E89.MirrorCS", {"start": v(15, -120) * mm, "mid": v(0, -135) * mm, "end": v(-15, -120) * mm});
            skLineSegment(sketch, "E90.MirrorCS", {"start": v(-15, -108) * mm, "end": v(-33, -90) * mm});
            skLineSegment(sketch, "E91.MirrorCS", {"start": v(15, -120) * mm, "end": v(15, -108) * mm});
            skCircle(sketch, "E92.MirrorC", {"center": v(0, -120) * mm, "radius": 6 * mm});
            skLineSegment(sketch, "E93.MirrorCS", {"start": v(0, -90) * mm, "end": v(0, -120) * mm, "construction": true});
            skSolve(sketch);
        }
        {
            var Q0;
            Q0=makeQuery(id+"F16.imprint","IMPRINT",FACE,{"disambiguationData":[TD([[makeQuery(id+"F16.imprint","IMPRINT",EDGE,{"derivedFrom":makeQuery(id+"F1.opExtrude","CAP_EDGE",EDGE,{"disambiguationData":[OSD([sQuery(id+"F0.wireOp",EDGE,"E1.left")])],"isStart":true})}),-1.0]])]});
            var Q1;
            Q1=makeQuery(id+"F16.imprint","IMPRINT",FACE,{"disambiguationData":[TD([[makeQuery(id+"F16.imprint","IMPRINT",EDGE,{"derivedFrom":sQuery(id+"F16.wireOp",EDGE,"E87.MirrorCS")}),-1.0]])]});
            var Q2;
            Q2=makeQuery(id+"F16.imprint","IMPRINT",FACE,{"disambiguationData":[TD([[makeQuery(id+"F16.imprint","IMPRINT",EDGE,{"derivedFrom":sQuery(id+"F16.wireOp",EDGE,"E80")}),-1.0]])]});
            var Q3;
            Q3=makeQuery(id+"F2.opExtrude","CAP_FACE",FACE,{"disambiguationData":[OSD([sQuery(id+"F0.wireOp",EDGE,"E12"),sQuery(id+"F0.wireOp",EDGE,"E13"),sQuery(id+"F0.wireOp",EDGE,"E14"),sQuery(id+"F0.wireOp",EDGE,"E15"),sQuery(id+"F0.wireOp",EDGE,"E17.filletArc"),sQuery(id+"F0.wireOp",EDGE,"E18.filletArc"),sQuery(id+"F0.wireOp",EDGE,"E19.filletArc"),sQuery(id+"F0.wireOp",EDGE,"E20.filletArc"),sQuery(id+"F0.wireOp",EDGE,"E25.0"),sQuery(id+"F0.wireOp",EDGE,"E25.1"),sQuery(id+"F0.wireOp",EDGE,"E25.2"),sQuery(id+"F0.wireOp",EDGE,"E25.3"),sQuery(id+"F0.wireOp",EDGE,"E25.4"),sQuery(id+"F0.wireOp",EDGE,"E25.5"),sQuery(id+"F0.wireOp",EDGE,"E25.6"),sQuery(id+"F0.wireOp",EDGE,"E25.7")])],"isStart":false});
            extrude(context, id + "F17", {"entities" : qUnion([Q0, Q1, Q2]), "endBound" : BoundingType.UP_TO_SURFACE, "depth" : 25 * mm, "endBoundEntityFace" : qUnion([Q3]), "offsetDistance" : 25 * mm});
        }
    });
